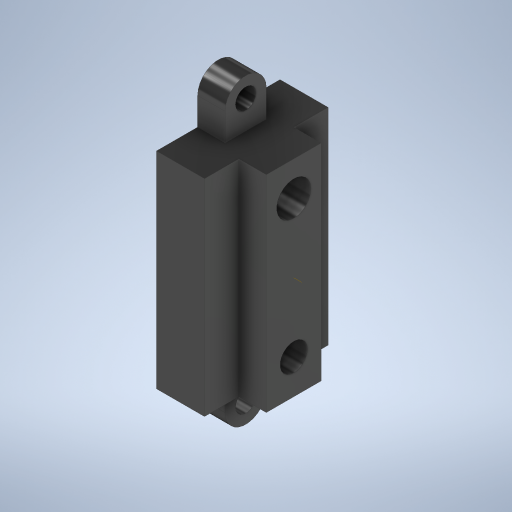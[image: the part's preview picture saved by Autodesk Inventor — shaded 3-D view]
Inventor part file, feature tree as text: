
AUTODESK INVENTOR PART (.ipt)
format: ipt  version: 2023 (Build 270158000, 158)  size: 296,960 bytes
history: native  units: mm
features: sketch x6, extrude x3, hole x3, mirror x1
ambient origin geometry x8: Origin, YZ Plane, XZ Plane, XY Plane, X Axis, Y Axis, Z Axis, Center Point
bodies: Volumenkörper1 (feature_tree)
feature tree (13):
  extrude  "Extrusion1"  Depth=18.0mm
  extrude  "Extrusion2"  Depth=8.0mm
  hole  "Bohrung1"  [1 undecoded]
  hole  "Bohrung2"  [1 undecoded]
  extrude  "Extrusion3"  Depth=10.0mm
  hole  "Bohrung3"  [1 undecoded]
  mirror  "Spiegeln1"
  sketch  "Skizze1"  dims[d0=30.0mm d1=18.0mm]
  sketch  "Skizze2"  dims[d2=7.0mm d3=0.0mm d4=8.0mm]
  sketch  "Skizze3"  dims[d5=30.0mm d6=4.0mm d7=0.0mm]
  sketch  "Skizze4"  dims[d8=5.0mm d9=6.0mm d10=4.0mm d11=2.0mm d12=90.0deg d13=4.0mm d14=20.594885mm]
  sketch  "Skizze5"  dims[d15=4.0mm d16=6.0mm d17=4.0mm d18=2.0mm d19=90.0deg d20=4.0mm d21=20.594885mm d22=0.0mm]
  sketch  "Skizze6"  dims[d23=5.0mm d24=10.0mm d25=4.0mm d26=90.0deg d27=3.0mm d28=3.0mm d29=4.0mm d30=0.0mm d31=3.0mm d32=6.0mm d33=4.0mm d34=2.0mm d35=90.0deg d36=4.0mm d37=20.594885mm d38=0.0mm]
note: 3 required parameter values undecoded (feature->parameter linkage not recoverable at this tier; creation-order binding heuristic only, values carry confidence <= 0.55)
